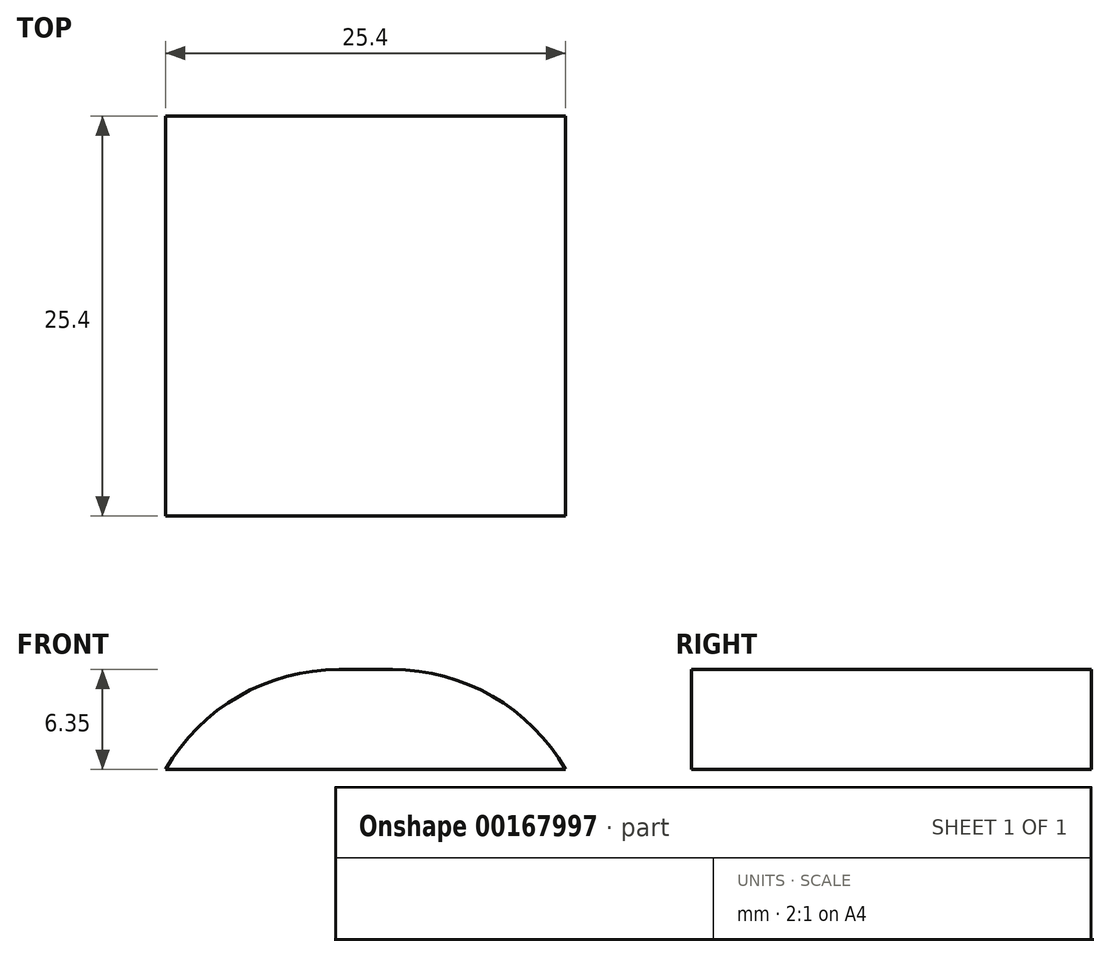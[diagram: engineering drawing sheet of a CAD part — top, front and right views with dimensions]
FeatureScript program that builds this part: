
annotation { "Feature Type Name" : "Feature", "Feature Type Description" : "" }
export const myFeature = defineFeature(function(context is Context, id is Id, definition is map)
    precondition{}
    {
        {
            var Q0;
            Q0=qCreatedBy(makeId("Front.planeOp"),FACE);
            var sketch = newSketch(context, id + "F0", { "sketchPlane" : qUnion([Q0])});
            skLineSegment(sketch, "E0.bottom", {"start": v(-38.69, 12.7) * mm, "end": v(12.11, 12.7) * mm});
            skLineSegment(sketch, "E0.top", {"start": v(-38.69, -12.7) * mm, "end": v(12.11, -12.7) * mm});
            skLineSegment(sketch, "E0.left", {"start": v(-38.69, 12.7) * mm, "end": v(-38.69, -12.7) * mm});
            skLineSegment(sketch, "E0.right", {"start": v(12.11, 12.7) * mm, "end": v(12.11, -12.7) * mm});
            skLineSegment(sketch, "E1.bottom", {"start": v(-13.29, 12.7) * mm, "end": v(12.11, 12.7) * mm});
            skLineSegment(sketch, "E1.top", {"start": v(-13.29, 6.35) * mm, "end": v(12.11, 6.35) * mm});
            skLineSegment(sketch, "E1.left", {"start": v(-13.29, 12.7) * mm, "end": v(-13.29, 6.35) * mm});
            skLineSegment(sketch, "E1.right", {"start": v(12.11, 12.7) * mm, "end": v(12.11, 6.35) * mm});
            skLineSegment(sketch, "E2.bottom", {"start": v(-13.29, -12.7) * mm, "end": v(12.11, -12.7) * mm});
            skLineSegment(sketch, "E2.top", {"start": v(-13.29, -6.35) * mm, "end": v(12.11, -6.35) * mm});
            skLineSegment(sketch, "E2.left", {"start": v(-13.29, -12.7) * mm, "end": v(-13.29, -6.35) * mm});
            skLineSegment(sketch, "E2.right", {"start": v(12.11, -12.7) * mm, "end": v(12.11, -6.35) * mm});
            skCircle(sketch, "E3", {"center": v(-25.99, 0) * mm, "radius": 10.16 * mm});
            skSolve(sketch);
        }
        {
            var Q0;
            Q0=makeQuery(id+"F0.imprint","IMPRINT",FACE,{"disambiguationData":[TD([[makeQuery(id+"F0.imprint","IMPRINT",EDGE,{"derivedFrom":sQuery(id+"F0.wireOp",EDGE,"E0.bottom")}),-1.0]])]});
            extrude(context, id + "F1", {"entities" : qUnion([Q0]), "depth" : 25.4 * mm});
        }
        {
            var Q0;
            Q0=makeQuery(id+"F1.opExtrude","SWEPT_EDGE",EDGE,{"disambiguationData":[OSD([sQuery(id+"F0.wireOp",EDGE,"E0.bottom"),sQuery(id+"F0.wireOp",EDGE,"E1.bottom"),sQuery(id+"F0.wireOp",EDGE,"E1.left")])]});
            var Q1;
            Q1=makeQuery(id+"F1.opExtrude","SWEPT_EDGE",EDGE,{"disambiguationData":[OSD([sQuery(id+"F0.wireOp",EDGE,"E0.bottom"),sQuery(id+"F0.wireOp",EDGE,"E0.left")])]});
            var Q2;
            Q2=makeQuery(id+"F1.opExtrude","SWEPT_EDGE",EDGE,{"disambiguationData":[OSD([sQuery(id+"F0.wireOp",EDGE,"E0.top"),sQuery(id+"F0.wireOp",EDGE,"E2.bottom"),sQuery(id+"F0.wireOp",EDGE,"E2.left")])]});
            var Q3;
            Q3=makeQuery(id+"F1.opExtrude","SWEPT_EDGE",EDGE,{"disambiguationData":[OSD([sQuery(id+"F0.wireOp",EDGE,"E0.top"),sQuery(id+"F0.wireOp",EDGE,"E0.left")])]});
            fillet(context, id + "F2", {"entities" : qUnion([Q0, Q1, Q2, Q3]), "radius" : 12.7 * mm, "tangentPropagation" : true, "allowEdgeOverflow" : false});
        }
    });
